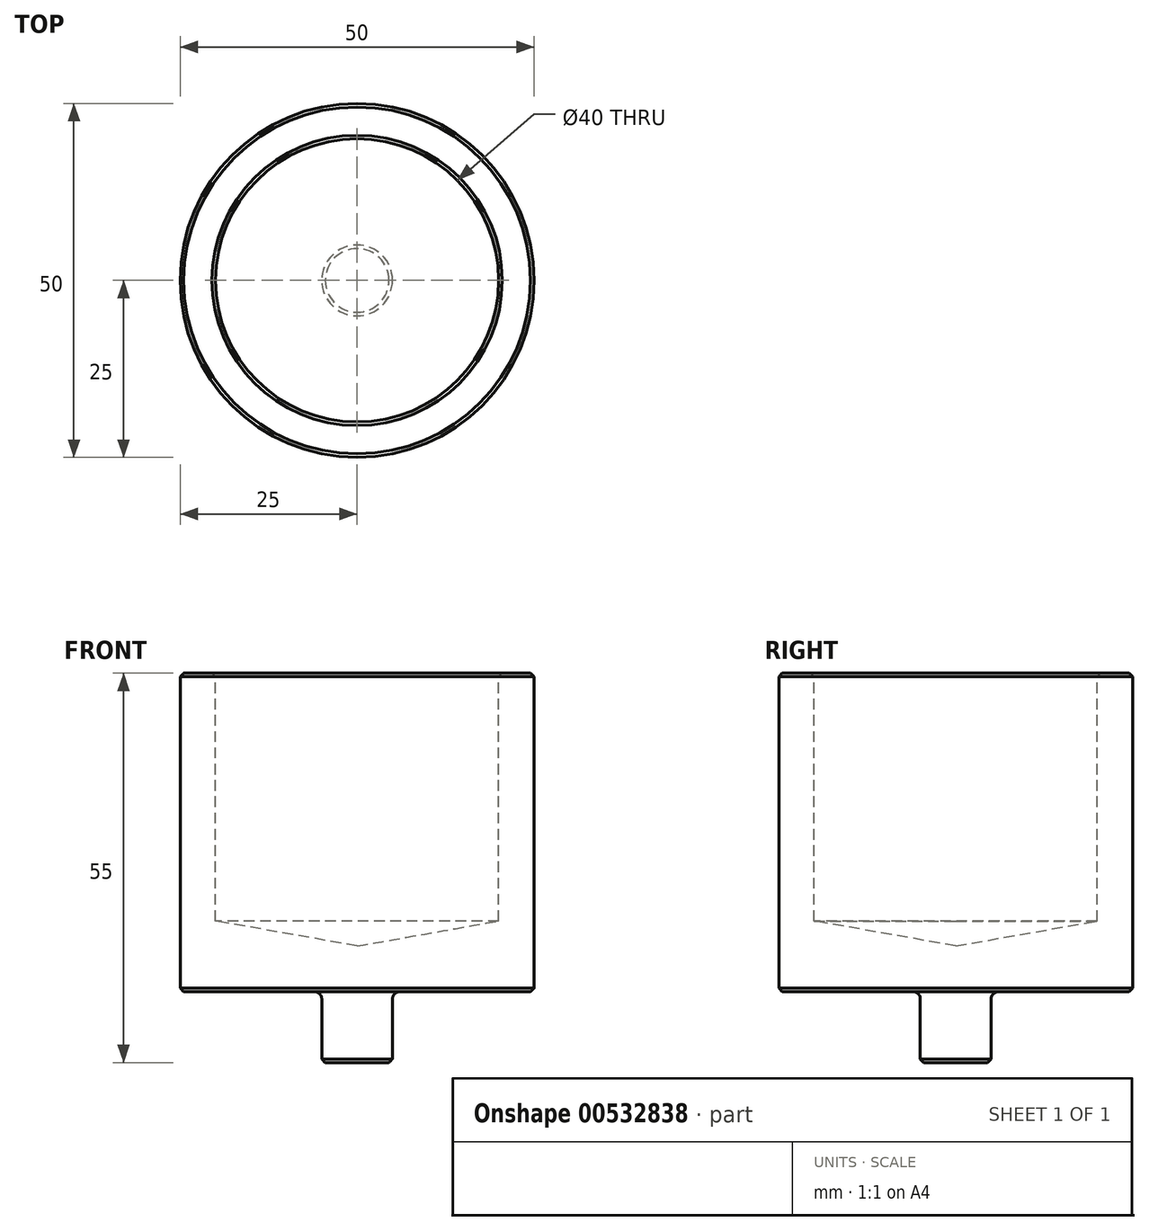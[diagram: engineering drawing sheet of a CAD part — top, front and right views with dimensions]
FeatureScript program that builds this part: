
annotation { "Feature Type Name" : "Feature", "Feature Type Description" : "" }
export const myFeature = defineFeature(function(context is Context, id is Id, definition is map)
    precondition{}
    {
        {
            var Q0;
            Q0=qCreatedBy(makeId("Front.planeOp"),FACE);
            var sketch = newSketch(context, id + "F0", { "sketchPlane" : qUnion([Q0])});
            skLineSegment(sketch, "E0", {"start": v(0, -10) * mm, "end": v(-5, -10) * mm});
            skLineSegment(sketch, "E1", {"start": v(-5, -10) * mm, "end": v(-5, 0) * mm});
            skLineSegment(sketch, "E2", {"start": v(-5, 0) * mm, "end": v(-25, 0) * mm});
            skLineSegment(sketch, "E3", {"start": v(-25, 0) * mm, "end": v(-25, 45) * mm});
            skLineSegment(sketch, "E4", {"start": v(-25, 45) * mm, "end": v(-20, 45) * mm});
            skLineSegment(sketch, "E5", {"start": v(-20, 45) * mm, "end": v(-20, 10) * mm});
            skLineSegment(sketch, "E6", {"start": v(-20, 10) * mm, "end": v(0, 6.47) * mm});
            skLineSegment(sketch, "E7", {"start": v(0, 6.47) * mm, "end": v(0, -10) * mm});
            skSolve(sketch);
        }
        {
            var Q0;
            Q0=makeQuery(id+"F0.imprint","IMPRINT",FACE,{"disambiguationData":[TD([[makeQuery(id+"F0.imprint","IMPRINT",EDGE,{"derivedFrom":sQuery(id+"F0.wireOp",EDGE,"E0")}),-1.0]])]});
            var Q1;
            Q1=sQuery(id+"F0.wireOp",EDGE,"E7");
            revolve(context, id + "F1", {"entities" : qUnion([Q0]), "axis" : qUnion([Q1]), "revolveType" : RevolveType.FULL});
        }
        {
            var Q0;
            Q0=makeQuery(id+"F1.opRevolve","SWEPT_EDGE",EDGE,{"disambiguationData":[OSD([sQuery(id+"F0.wireOp",EDGE,"E1"),sQuery(id+"F0.wireOp",EDGE,"E2")])]});
            fillet(context, id + "F2", {"entities" : qUnion([Q0]), "radius" : 1 * mm, "tangentPropagation" : true, "allowEdgeOverflow" : false});
        }
        {
            var Q0;
            Q0=makeQuery(id+"F1.opRevolve","SWEPT_EDGE",EDGE,{"disambiguationData":[OSD([sQuery(id+"F0.wireOp",EDGE,"E0"),sQuery(id+"F0.wireOp",EDGE,"E1")])]});
            var Q1;
            Q1=makeQuery(id+"F1.opRevolve","SWEPT_EDGE",EDGE,{"disambiguationData":[OSD([sQuery(id+"F0.wireOp",EDGE,"E2"),sQuery(id+"F0.wireOp",EDGE,"E3")])]});
            var Q2;
            Q2=makeQuery(id+"F1.opRevolve","SWEPT_EDGE",EDGE,{"disambiguationData":[OSD([sQuery(id+"F0.wireOp",EDGE,"E3"),sQuery(id+"F0.wireOp",EDGE,"E4")])]});
            var Q3;
            Q3=makeQuery(id+"F1.opRevolve","SWEPT_EDGE",EDGE,{"disambiguationData":[OSD([sQuery(id+"F0.wireOp",EDGE,"E4"),sQuery(id+"F0.wireOp",EDGE,"E5")])]});
            chamfer(context, id + "F3", {"entities" : qUnion([Q0, Q1, Q2, Q3]), "width" : 0.5 * mm, "tangentPropagation" : true});
        }
    });
